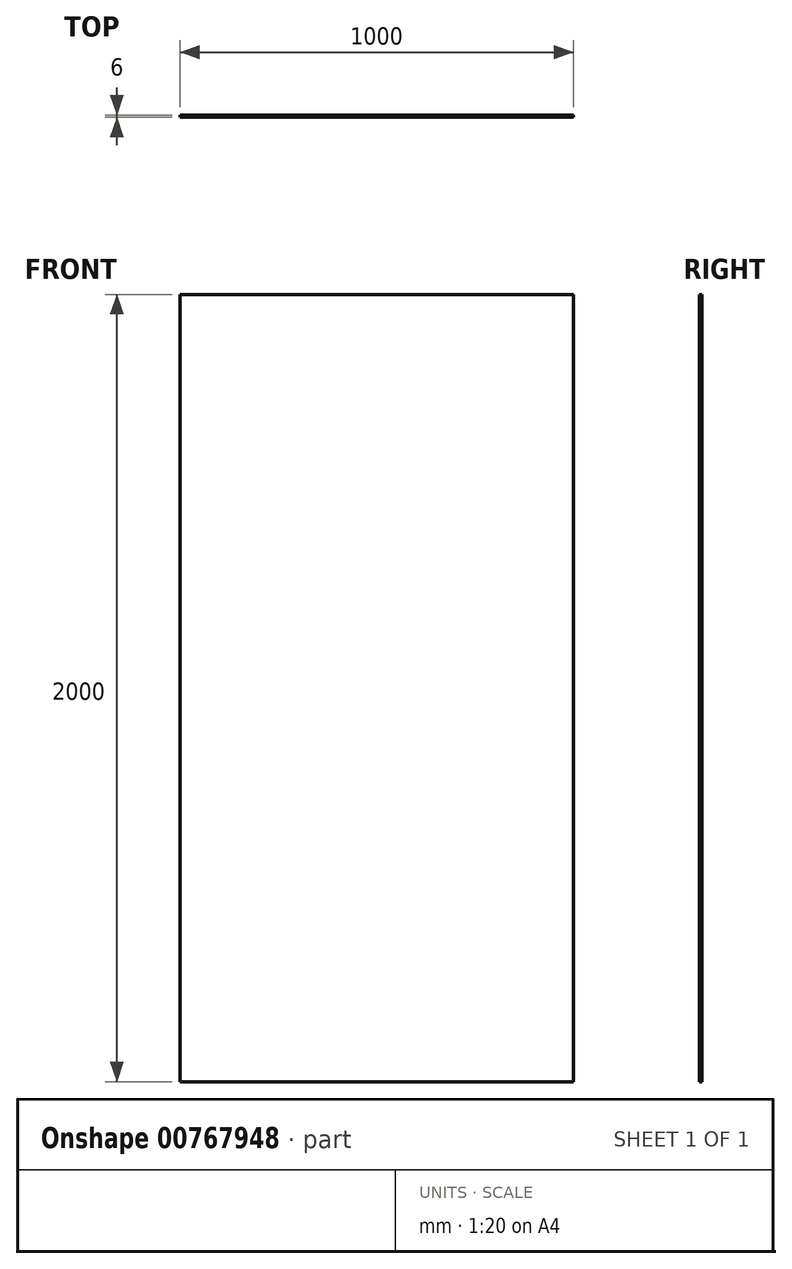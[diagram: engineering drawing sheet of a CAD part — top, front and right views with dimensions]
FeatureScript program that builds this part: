
annotation { "Feature Type Name" : "Feature", "Feature Type Description" : "" }
export const myFeature = defineFeature(function(context is Context, id is Id, definition is map)
    precondition{}
    {
        {
            var Q0;
            Q0=qCreatedBy(makeId("Front.planeOp"),FACE);
            var sketch = newSketch(context, id + "F0", { "sketchPlane" : qUnion([Q0])});
            skLineSegment(sketch, "E0.bottom", {"start": v(-909.3, 1896.64) * mm, "end": v(90.7, 1896.64) * mm});
            skLineSegment(sketch, "E0.top", {"start": v(-909.3, -103.36) * mm, "end": v(90.7, -103.36) * mm});
            skLineSegment(sketch, "E0.left", {"start": v(-909.3, 1896.64) * mm, "end": v(-909.3, -103.36) * mm});
            skLineSegment(sketch, "E0.right", {"start": v(90.7, 1896.64) * mm, "end": v(90.7, -103.36) * mm});
            skSolve(sketch);
        }
        {
            var Q0;
            Q0 = qSketchRegion(id + "F0", true);
            extrude(context, id + "F1", {"entities" : qUnion([Q0]), "depth" : 6 * mm, "offsetDistance" : 25 * mm});
        }
    });
